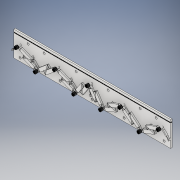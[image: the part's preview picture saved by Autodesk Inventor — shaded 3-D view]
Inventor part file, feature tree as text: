
AUTODESK INVENTOR PART (.ipt)
format: ipt  version: 2019 (Build 230136000, 136)  size: 1,205,248 bytes
history: native  units: mm
features: other x10, sketch x10, extrude x10, plane x5, pattern_linear x4, mirror x2, direct_edit x1
ambient origin geometry x8: Origin, YZ Plane, XZ Plane, XY Plane, X Axis, Y Axis, Z Axis, Center Point
bodies: Body1 (feature_tree), Body2 (feature_tree)
feature tree (42):
  plane  "Work Plane1"
  other  "iFeature13:4"
  other  "iFeature13:3"
  pattern_linear  "Rectangular Pattern20"  Count1=2  [1 undecoded]
  plane  "Work Plane2"
  sketch  "Sketch5"  dims[d58=-4.1mm]
  extrude  "Extrusion1"  Depth=10.0mm
  extrude  "Extrusion3"  Depth=10.0mm TaperAngle=360.0deg
  other  "iFeature2:1"
  other  "iFeature2:2"
  pattern_linear  "Rectangular Pattern21"  Spacing1=0.0mm  [1 undecoded]
  other  "iFeature3:1"
  other  "iFeature3:2"
  pattern_linear  "Rectangular Pattern22"  Count1=2  [1 undecoded]
  sketch  "Sketch19"  dims[d65=-5.1mm]
  extrude  "Extrusion9"  Depth=10.0mm
  sketch  "Sketch20"  dims[d66=4.0mm d67=0.0mm]
  extrude  "Extrusion10"  Depth=6.0mm TaperAngle=0.0deg
  sketch  "Sketch21"  dims[d119=108.0mm]
  extrude  "Extrusion11"  Depth=10.0mm
  plane  "Work Plane8"
  extrude  "Extrusion13"  Depth=6.0mm TaperAngle=0.0deg
  plane  "Work Plane9"
  plane  "Work Plane10"
  sketch  "Sketch26"  dims[d121=65.0mm]
  extrude  "Extrusion14"  Depth=10.0mm
  extrude  "Extrusion15"  Depth=6.0mm TaperAngle=0.0deg
  pattern_linear  "Rectangular Pattern23"  Spacing1=-2.0mm  [1 undecoded]
  sketch  "Sketch28"  dims[d149=2.0mm]
  extrude  "Extrusion16"  Depth=6.0mm
  mirror  "Mirror3"
  mirror  "Mirror4"
  direct_edit  "Direct Edit6"
  extrude  "Extrusion17"  Depth=10.0mm TaperAngle=0.0deg
  sketch  "Sketch24"  dims[d120=0.0mm]
  sketch  "Sketch27"  dims[d122=408.0mm]
  sketch  "Sketch29"  dims[d150=57.0mm]
  sketch  "Sketch30"  dims[d151=4.0mm d152=0.0mm d264=0.0mm d265=1.0mm d266=0.0mm d267=4.0mm d278=0.0mm d279=1.0mm d280=0.0mm d281=4.0mm d292=0.0mm d293=1.0mm d294=0.0mm d295=4.0mm d306=0.0mm d307=1.0mm d308=0.0mm d309=4.0mm d320=0.0mm d321=1.0mm d322=0.0mm d323=4.0mm d334=0.0mm d335=1.0mm d336=0.0mm d337=4.0mm d448=0.0mm d449=1.0mm d450=0.0mm d451=4.0mm d499=1.0mm d500=0.4mm d501=121.21mm d502=0.0mm d503=3.0mm d504=4.0mm d505=4.0mm d506=100.0mm d507=0.0mm d508=8.726646mm d509=0.0mm d510=1.0mm d511=0.0mm d512=4.0mm d513=20.0mm d515=100.0mm d516=20.0mm d518=100.0mm d536=0.5mm d537=0.5mm d538=121.21mm d539=0.0mm d540=85.0mm d541=35.0mm d542=9.0mm d543=8.0mm d544=4.0mm d545=4.0mm d546=10.0mm d547=8.726646mm d548=0.3mm d549=20.0mm d550=360.0deg d551=0.0mm d552=4.0mm d553=20.0mm d555=100.0mm d562=121.21mm d563=0.0mm d564=8.2mm d565=4.0mm d566=0.0mm d567=8.2mm d569=8.0mm d570=6.0mm d571=0.0mm d572=8.0mm d573=6.0mm d574=0.0mm d575=8.0mm d576=6.0mm d577=0.0mm d578=-2.0mm d582=6.0mm d583=2.0mm d584=0.0mm d585=-2.0mm d586=-2.0mm d588=6.0mm d589=6.0mm d590=2.0mm d591=0.0mm d592=2.0mm d593=0.0mm d594=20.0mm d596=100.0mm d597=10.0mm d598=0.0mm d599=12.0mm d600=10.0mm d601=10.0mm d602=6.5mm d603=74.0mm d604=225.0mm d605=20.0mm d607=125.0mm d608=10.0mm d610=10.0mm d612=20.0mm d614=225.0mm d615=10.0mm d617=10.0mm d619=20.0mm d621=325.0mm d622=10.0mm d624=10.0mm d626=20.0mm d628=450.0mm d629=10.0mm d631=10.0mm d633=6.5mm d634=75.0mm d635=50.0mm d636=40.0mm d638=100.0mm d639=10.0mm d641=10.0mm d643=6.5mm d644=50.0mm d645=0.0mm d646=6.5mm d647=50.0mm d648=0.0mm d649=10.0mm d650=0.0mm]
  other  "iFeature13:16"
  other  "Scale7"
  other  "iFeature3:4"
  other  "iFeature2:8"
note: 4 required parameter values undecoded (feature->parameter linkage not recoverable at this tier; creation-order binding heuristic only, values carry confidence <= 0.55)
